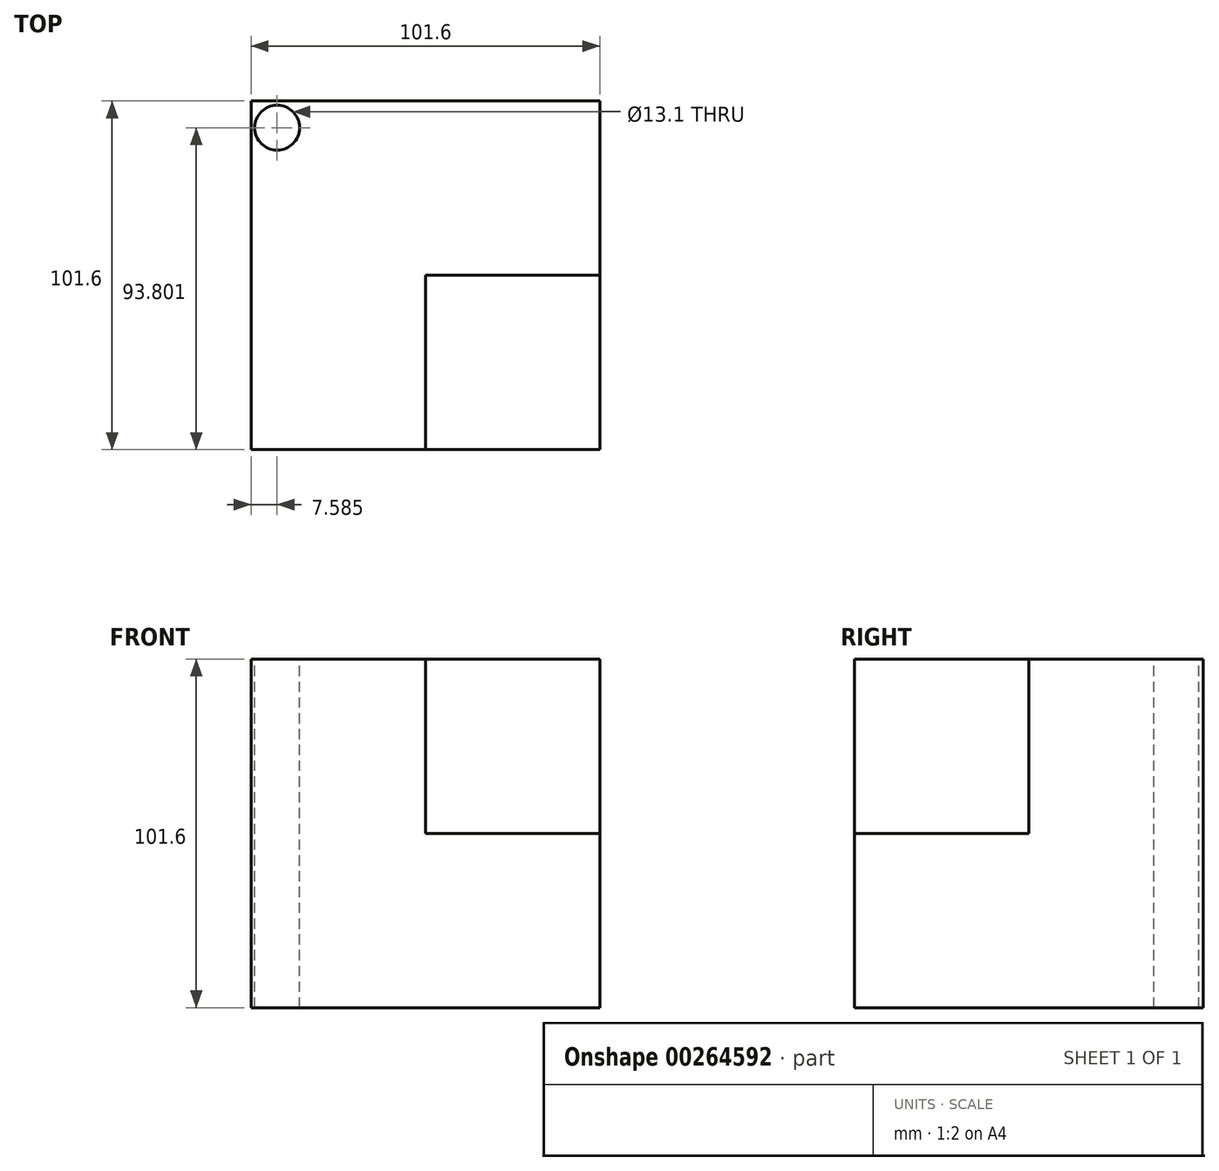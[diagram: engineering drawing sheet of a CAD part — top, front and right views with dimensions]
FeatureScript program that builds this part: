
annotation { "Feature Type Name" : "Feature", "Feature Type Description" : "" }
export const myFeature = defineFeature(function(context is Context, id is Id, definition is map)
    precondition{}
    {
        {
            var Q0;
            Q0=qCreatedBy(makeId("Front.planeOp"),FACE);
            var sketch = newSketch(context, id + "F0", { "sketchPlane" : qUnion([Q0])});
            skLineSegment(sketch, "E0.bottom", {"start": v(0, 0) * mm, "end": v(-101.6, 0) * mm});
            skLineSegment(sketch, "E0.top", {"start": v(0, 101.6) * mm, "end": v(-101.6, 101.6) * mm});
            skLineSegment(sketch, "E0.left", {"start": v(0, 0) * mm, "end": v(0, 101.6) * mm});
            skLineSegment(sketch, "E0.right", {"start": v(-101.6, 0) * mm, "end": v(-101.6, 101.6) * mm});
            skSolve(sketch);
        }
        {
            var Q0;
            Q0 = qSketchRegion(id + "F0", true);
            extrude(context, id + "F1", {"entities" : qUnion([Q0]), "depth" : 101.6 * mm});
        }
        {
            var Q0;
            Q0=makeQuery(id+"F1.opExtrude","SWEPT_FACE",FACE,{"disambiguationData":[OSD([sQuery(id+"F0.wireOp",EDGE,"E0.top")])]});
            var sketch = newSketch(context, id + "F2", { "sketchPlane" : qUnion([Q0])});
            skCircle(sketch, "E1", {"center": v(-94.01, -7.8) * mm, "radius": 6.55 * mm});
            skSolve(sketch);
        }
        {
            var Q0;
            Q0=makeQuery(id+"F2.imprint","IMPRINT",FACE,{"disambiguationData":[TD([[makeQuery(id+"F2.imprint","IMPRINT",EDGE,{"derivedFrom":sQuery(id+"F2.wireOp",EDGE,"E1")}),1.0]])]});
            extrude(context, id + "F3", {"entities" : qUnion([Q0]), "operationType" : NewBodyOperationType.REMOVE, "oppositeDirection" : true, "depth" : 101.6 * mm});
        }
        {
            var Q0;
            Q0=makeQuery(id+"F1.opExtrude","SWEPT_FACE",FACE,{"disambiguationData":[OSD([sQuery(id+"F0.wireOp",EDGE,"E0.top")])]});
            var sketch = newSketch(context, id + "F4", { "sketchPlane" : qUnion([Q0])});
            skLineSegment(sketch, "E2.bottom", {"start": v(0, -101.6) * mm, "end": v(-50.8, -101.6) * mm});
            skLineSegment(sketch, "E2.top", {"start": v(0, -50.8) * mm, "end": v(-50.8, -50.8) * mm});
            skLineSegment(sketch, "E2.left", {"start": v(0, -101.6) * mm, "end": v(0, -50.8) * mm});
            skLineSegment(sketch, "E2.right", {"start": v(-50.8, -101.6) * mm, "end": v(-50.8, -50.8) * mm});
            skSolve(sketch);
        }
        {
            var Q0;
            Q0 = qSketchRegion(id + "F4", true);
            extrude(context, id + "F5", {"entities" : qUnion([Q0]), "operationType" : NewBodyOperationType.REMOVE, "oppositeDirection" : true, "depth" : 50.8 * mm});
        }
    });
